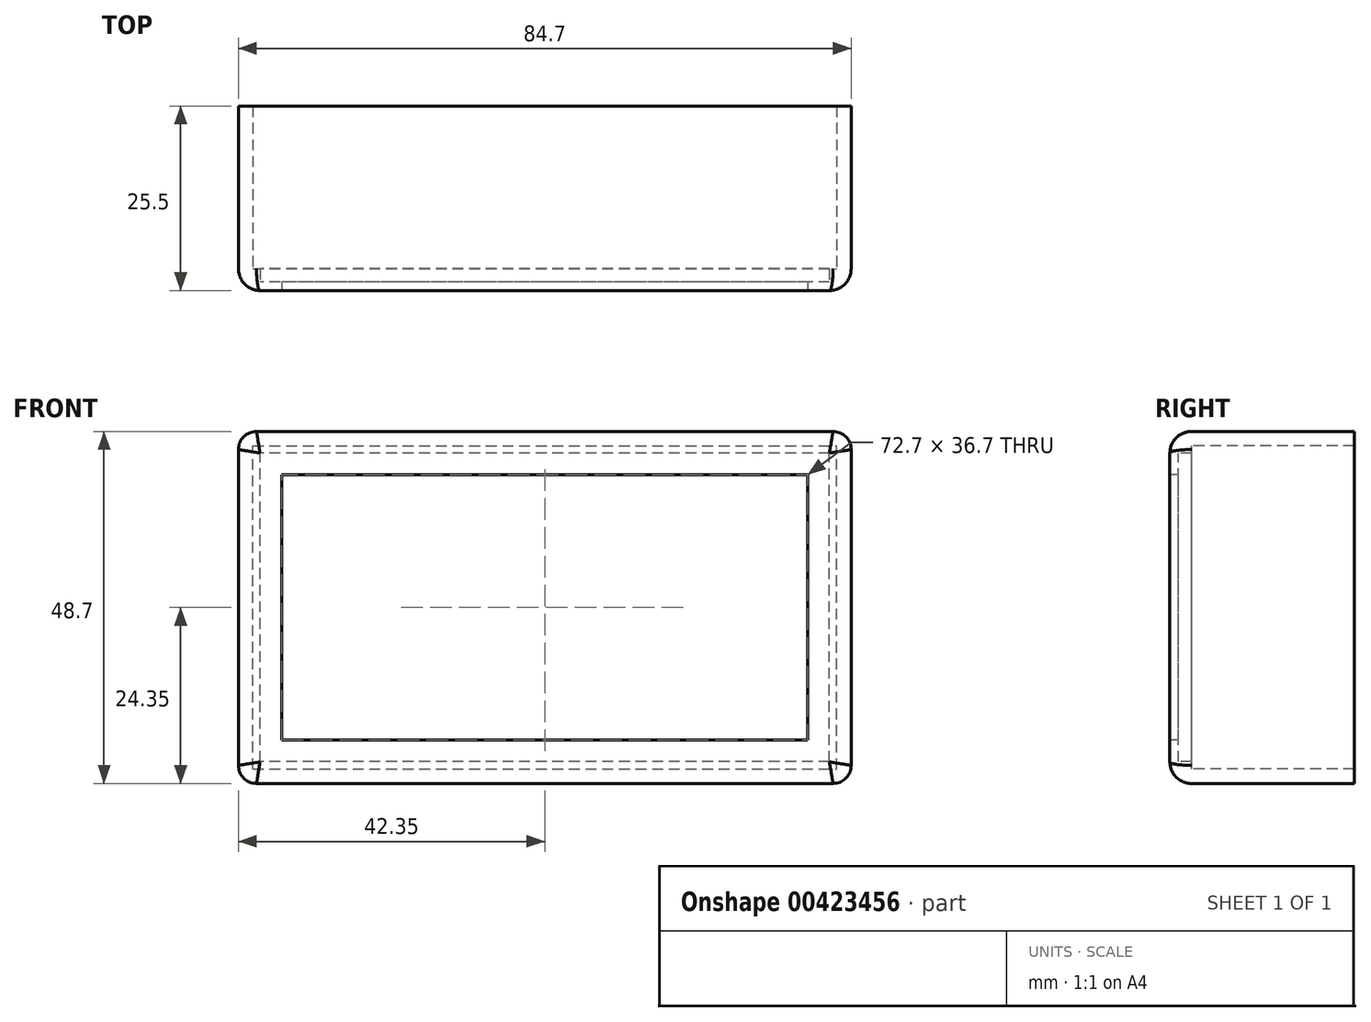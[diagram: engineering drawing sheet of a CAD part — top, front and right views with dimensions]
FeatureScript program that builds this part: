
annotation { "Feature Type Name" : "Feature", "Feature Type Description" : "" }
export const myFeature = defineFeature(function(context is Context, id is Id, definition is map)
    precondition{}
    {
        {
            var Q0;
            Q0=qCreatedBy(makeId("Front.planeOp"),FACE);
            var sketch = newSketch(context, id + "F0", { "sketchPlane" : qUnion([Q0])});
            skLineSegment(sketch, "E0.bottom", {"start": v(0, 0) * mm, "end": v(80.7, 0) * mm});
            skLineSegment(sketch, "E0.top", {"start": v(0, 44.7) * mm, "end": v(80.7, 44.7) * mm});
            skLineSegment(sketch, "E0.left", {"start": v(0, 0) * mm, "end": v(0, 44.7) * mm});
            skLineSegment(sketch, "E0.right", {"start": v(80.7, 0) * mm, "end": v(80.7, 44.7) * mm});
            skLineSegment(sketch, "E1.bottom", {"start": v(76.7, 4) * mm, "end": v(4, 4) * mm});
            skLineSegment(sketch, "E1.top", {"start": v(76.7, 40.7) * mm, "end": v(4, 40.7) * mm});
            skLineSegment(sketch, "E1.left", {"start": v(76.7, 4) * mm, "end": v(76.7, 40.7) * mm});
            skLineSegment(sketch, "E1.right", {"start": v(4, 4) * mm, "end": v(4, 40.7) * mm});
            skLineSegment(sketch, "E2.bottom", {"start": v(80.2, -2) * mm, "end": v(0.5, -2) * mm});
            skLineSegment(sketch, "E2.top", {"start": v(80.2, 46.7) * mm, "end": v(0.5, 46.7) * mm});
            skLineSegment(sketch, "E2.left", {"start": v(82.7, 0.5) * mm, "end": v(82.7, 44.2) * mm});
            skLineSegment(sketch, "E2.right", {"start": v(-2, 0.5) * mm, "end": v(-2, 44.2) * mm});
            skPoint(sketch, "E3.visualSharp", {"position": v(82.7, -2) * mm});
            skArc(sketch, "E3.filletArc", {"start": v(80.2, -2) * mm, "mid": v(81.97, -1.27) * mm, "end": v(82.7, 0.5) * mm});
            skPoint(sketch, "E4.visualSharp", {"position": v(82.7, 46.7) * mm});
            skArc(sketch, "E4.filletArc", {"start": v(82.7, 44.2) * mm, "mid": v(81.97, 45.97) * mm, "end": v(80.2, 46.7) * mm});
            skPoint(sketch, "E5.visualSharp", {"position": v(-2, 46.7) * mm});
            skArc(sketch, "E5.filletArc", {"start": v(0.5, 46.7) * mm, "mid": v(-1.27, 45.97) * mm, "end": v(-2, 44.2) * mm});
            skPoint(sketch, "E6.visualSharp", {"position": v(-2, -2) * mm});
            skArc(sketch, "E6.filletArc", {"start": v(-2, 0.5) * mm, "mid": v(-1.27, -1.27) * mm, "end": v(0.5, -2) * mm});
            skLineSegment(sketch, "E7.bottom", {"start": v(79.7, 1) * mm, "end": v(1, 1) * mm});
            skLineSegment(sketch, "E7.top", {"start": v(79.7, 43.7) * mm, "end": v(1, 43.7) * mm});
            skLineSegment(sketch, "E7.left", {"start": v(79.7, 1) * mm, "end": v(79.7, 43.7) * mm});
            skLineSegment(sketch, "E7.right", {"start": v(1, 1) * mm, "end": v(1, 43.7) * mm});
            skSolve(sketch);
        }
        {
            var Q0;
            Q0=makeQuery(id+"F0.imprint","IMPRINT",FACE,{"disambiguationData":[TD([[makeQuery(id+"F0.imprint","IMPRINT",EDGE,{"derivedFrom":sQuery(id+"F0.wireOp",EDGE,"E1.bottom")}),1.0]])]});
            extrude(context, id + "F1", {"entities" : qUnion([Q0]), "oppositeDirection" : true, "depth" : 1.2 * mm, "offsetDistance" : 25 * mm});
        }
        {
            var Q0;
            Q0=makeQuery(id+"F0.imprint","IMPRINT",FACE,{"disambiguationData":[TD([[makeQuery(id+"F0.imprint","IMPRINT",EDGE,{"derivedFrom":sQuery(id+"F0.wireOp",EDGE,"E0.bottom")}),1.0]])]});
            extrude(context, id + "F2", {"entities" : qUnion([Q0]), "operationType" : NewBodyOperationType.ADD, "oppositeDirection" : true, "depth" : 3 * mm, "offsetDistance" : 25 * mm});
        }
        {
            var Q0;
            Q0=makeQuery(id+"F0.imprint","IMPRINT",FACE,{"disambiguationData":[TD([[makeQuery(id+"F0.imprint","IMPRINT",EDGE,{"derivedFrom":sQuery(id+"F0.wireOp",EDGE,"E0.bottom")}),-1.0]])]});
            extrude(context, id + "F3", {"entities" : qUnion([Q0]), "operationType" : NewBodyOperationType.ADD, "oppositeDirection" : true, "depth" : 25.5 * mm, "offsetDistance" : 25 * mm});
        }
        {
            var Q0;
            Q0=makeQuery(id+"F3.opExtrude","CAP_EDGE",EDGE,{"disambiguationData":[OSD([sQuery(id+"F0.wireOp",EDGE,"E2.right")])],"isStart":true});
            var Q1;
            Q1=makeQuery(id+"F3.opExtrude","CAP_EDGE",EDGE,{"disambiguationData":[OSD([sQuery(id+"F0.wireOp",EDGE,"E2.bottom")])],"isStart":true});
            var Q2;
            Q2=makeQuery(id+"F3.opExtrude","CAP_EDGE",EDGE,{"disambiguationData":[OSD([sQuery(id+"F0.wireOp",EDGE,"E6.filletArc")])],"isStart":true});
            var Q3;
            Q3=makeQuery(id+"F3.opExtrude","CAP_EDGE",EDGE,{"disambiguationData":[OSD([sQuery(id+"F0.wireOp",EDGE,"E3.filletArc")])],"isStart":true});
            var Q4;
            Q4=makeQuery(id+"F3.opExtrude","CAP_EDGE",EDGE,{"disambiguationData":[OSD([sQuery(id+"F0.wireOp",EDGE,"E2.left")])],"isStart":true});
            var Q5;
            Q5=makeQuery(id+"F3.opExtrude","CAP_EDGE",EDGE,{"disambiguationData":[OSD([sQuery(id+"F0.wireOp",EDGE,"E4.filletArc")])],"isStart":true});
            var Q6;
            Q6=makeQuery(id+"F3.opExtrude","CAP_EDGE",EDGE,{"disambiguationData":[OSD([sQuery(id+"F0.wireOp",EDGE,"E2.top")])],"isStart":true});
            var Q7;
            Q7=makeQuery(id+"F3.opExtrude","CAP_EDGE",EDGE,{"disambiguationData":[OSD([sQuery(id+"F0.wireOp",EDGE,"E5.filletArc")])],"isStart":true});
            fillet(context, id + "F4", {"entities" : qUnion([Q0, Q1, Q2, Q3, Q4, Q5, Q6, Q7]), "radius" : 3 * mm, "allowEdgeOverflow" : false});
        }
    });
